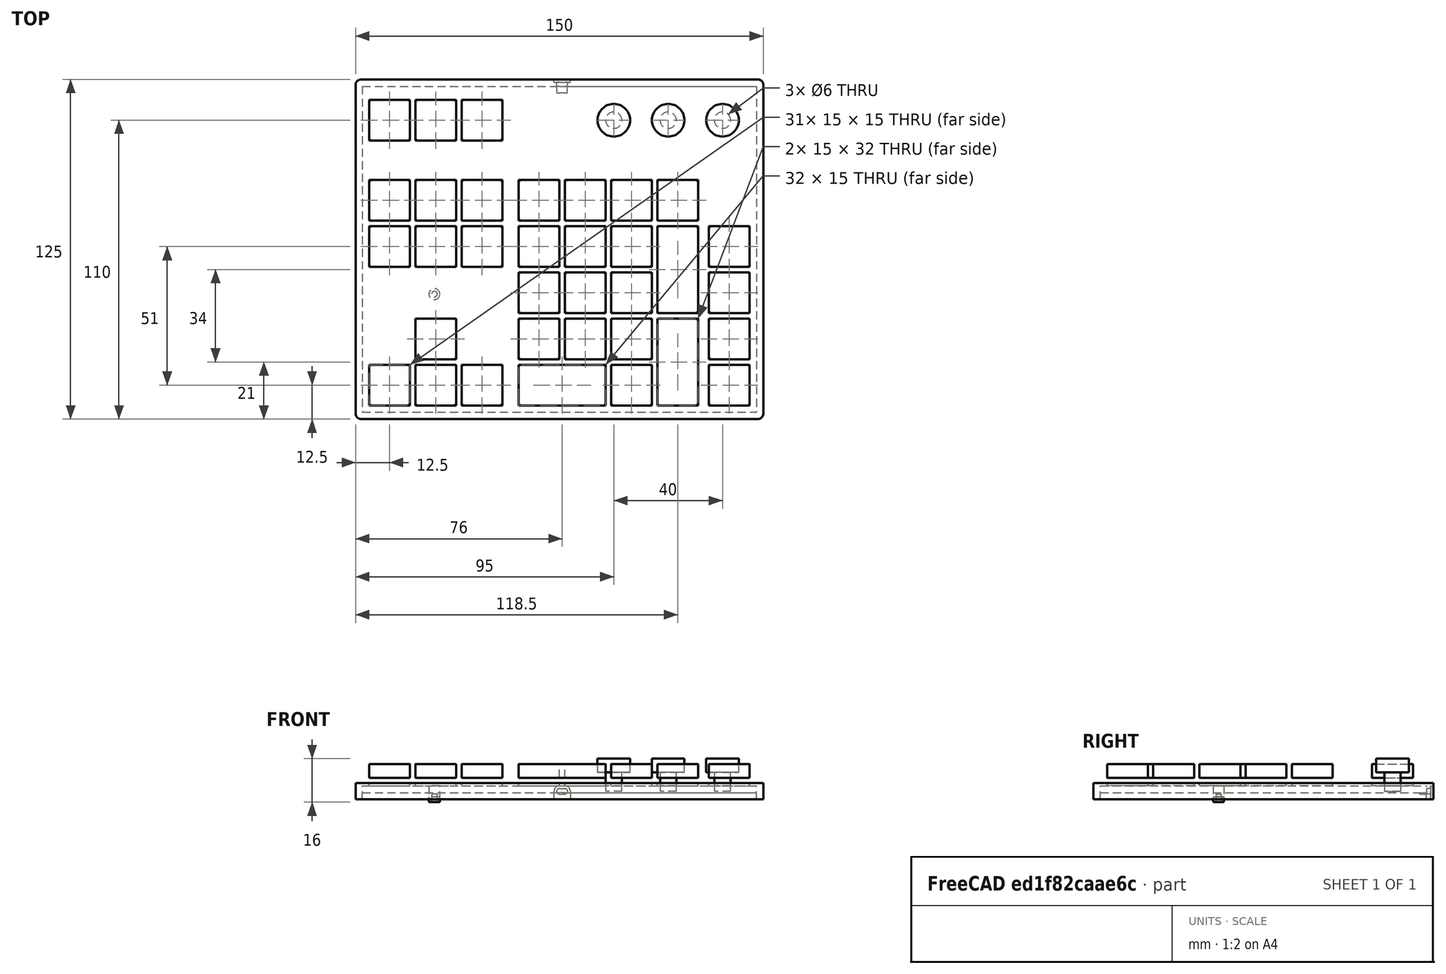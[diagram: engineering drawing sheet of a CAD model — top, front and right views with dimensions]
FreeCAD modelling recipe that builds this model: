
FCSTD DOCUMENT  (FreeCAD 1.0R39109 (Git))
Label: control
License: All rights reserved
LicenseURL: https://en.wikipedia.org/wiki/All_rights_reserved
objects: Part::Box×76, Part::Cut×42, Part::Fillet×35, Part::Cylinder×18, App::DocumentObjectGroup×5, Part::MultiFuse×3
note: 174 computed .brp shape members not serialized (recipe doc carries the construction recipe); baked Part::Feature solids carry a one-line shape summary decoded from their .brp

FEATURE [Part::Box] Box002  label="Down-S"
  AttacherType = Attacher::AttachEngine3D
  Height = 5
  Length = 15
  Placement = pos=(22,5,12) rot=(0,0,1;0rad)
  Width = 15
FEATURE [Part::Box] Box003  label="Up-S"
  AttacherType = Attacher::AttachEngine3D
  Height = 5
  Length = 15
  Placement = pos=(22,22,12) rot=(0,0,1;0rad)
  Width = 15
FEATURE [Part::Box] Box004  label="Right-S"
  AttacherType = Attacher::AttachEngine3D
  Height = 5
  Length = 15
  Placement = pos=(39,5,12) rot=(0,0,1;0rad)
  Width = 15
FEATURE [Part::Box] Box005  label="Zero/Insert-S"
  AttacherType = Attacher::AttachEngine3D
  Height = 5
  Length = 32
  Placement = pos=(60,5,12) rot=(0,0,1;0rad)
  Width = 15
FEATURE [Part::Box] Box006  label="Delete-S"
  AttacherType = Attacher::AttachEngine3D
  Height = 5
  Length = 15
  Placement = pos=(94,5,12) rot=(0,0,1;0rad)
  Width = 15
FEATURE [Part::Box] Box007  label="Left-S"
  AttacherType = Attacher::AttachEngine3D
  Height = 5
  Length = 15
  Placement = pos=(5,5,12) rot=(0,0,1;0rad)
  Width = 15
FEATURE [Part::Box] Box  label="Platform"
  AttacherType = Attacher::AttachEngine3D
  Height = 10
  Length = 150
  Width = 125
FEATURE [Part::Box] Box008  label="End-S"
  AttacherType = Attacher::AttachEngine3D
  Height = 5
  Length = 15
  Placement = pos=(130,5,12) rot=(0,0,1;0rad)
  Width = 15
FEATURE [Part::Fillet] Fillet
  Base = -> Box
  EdgeLinks = -> Box [Edge1,Edge3,Edge5,Edge7]
  Edges = 4 edges r=2: [Edge1,Edge3,Edge5,Edge7]
FEATURE [Part::Box] Box009  label="One-S"
  AttacherType = Attacher::AttachEngine3D
  Height = 5
  Length = 15
  Placement = pos=(60,22,12) rot=(0,0,1;0rad)
  Width = 15
FEATURE [Part::Box] Box010  label="Two-S"
  AttacherType = Attacher::AttachEngine3D
  Height = 5
  Length = 15
  Placement = pos=(77,22,12) rot=(0,0,1;0rad)
  Width = 15
FEATURE [Part::Box] Box011  label="Three-S"
  AttacherType = Attacher::AttachEngine3D
  Height = 5
  Length = 15
  Placement = pos=(94,22,12) rot=(0,0,1;0rad)
  Width = 15
FEATURE [Part::Box] Box012  label="Four-S"
  AttacherType = Attacher::AttachEngine3D
  Height = 5
  Length = 15
  Placement = pos=(60,39,12) rot=(0,0,1;0rad)
  Width = 15
FEATURE [Part::Box] Box013  label="Five-S"
  AttacherType = Attacher::AttachEngine3D
  Height = 5
  Length = 15
  Placement = pos=(77,39,12) rot=(0,0,1;0rad)
  Width = 15
FEATURE [Part::Box] Box014  label="Six-S"
  AttacherType = Attacher::AttachEngine3D
  Height = 5
  Length = 15
  Placement = pos=(94,39,12) rot=(0,0,1;0rad)
  Width = 15
FEATURE [Part::Box] Box015  label="Nine-S"
  AttacherType = Attacher::AttachEngine3D
  Height = 5
  Length = 15
  Placement = pos=(94,56,12) rot=(0,0,1;0rad)
  Width = 15
FEATURE [Part::Box] Box016  label="Eight-S"
  AttacherType = Attacher::AttachEngine3D
  Height = 5
  Length = 15
  Placement = pos=(77,56,12) rot=(0,0,1;0rad)
  Width = 15
FEATURE [Part::Box] Box017  label="Seven-S"
  AttacherType = Attacher::AttachEngine3D
  Height = 5
  Length = 15
  Placement = pos=(60,56,12) rot=(0,0,1;0rad)
  Width = 15
FEATURE [Part::Box] Box018  label="Numlock-S"
  AttacherType = Attacher::AttachEngine3D
  Height = 5
  Length = 15
  Placement = pos=(60,73,12) rot=(0,0,1;0rad)
  Width = 15
FEATURE [Part::Box] Box019  label="Divide-S"
  AttacherType = Attacher::AttachEngine3D
  Height = 5
  Length = 15
  Placement = pos=(77,73,12) rot=(0,0,1;0rad)
  Width = 15
FEATURE [Part::Box] Box020  label="Multi-S"
  AttacherType = Attacher::AttachEngine3D
  Height = 5
  Length = 15
  Placement = pos=(94,73,12) rot=(0,0,1;0rad)
  Width = 15
FEATURE [Part::Box] Box021  label="Enter-S"
  AttacherType = Attacher::AttachEngine3D
  Height = 5
  Length = 15
  Placement = pos=(111,5,12) rot=(0,0,1;0rad)
  Width = 32
FEATURE [Part::Box] Box022  label="PgDn-S"
  AttacherType = Attacher::AttachEngine3D
  Height = 5
  Length = 15
  Placement = pos=(130,22,12) rot=(0,0,1;0rad)
  Width = 15
FEATURE [Part::Box] Box023  label="Plus-S"
  AttacherType = Attacher::AttachEngine3D
  Height = 5
  Length = 15
  Placement = pos=(111,39,12) rot=(0,0,1;0rad)
  Width = 32
FEATURE [Part::Box] Box024  label="Minus-S"
  AttacherType = Attacher::AttachEngine3D
  Height = 5
  Length = 15
  Placement = pos=(111,73,12) rot=(0,0,1;0rad)
  Width = 15
FEATURE [Part::Box] Box025  label="PgUp-S"
  AttacherType = Attacher::AttachEngine3D
  Height = 5
  Length = 15
  Placement = pos=(130,39,12) rot=(0,0,1;0rad)
  Width = 15
FEATURE [Part::Box] Box026  label="Home-S"
  AttacherType = Attacher::AttachEngine3D
  Height = 5
  Length = 15
  Placement = pos=(130,56,12) rot=(0,0,1;0rad)
  Width = 15
FEATURE [Part::Box] Box027  label="M3"
  AttacherType = Attacher::AttachEngine3D
  Height = 5
  Length = 15
  Placement = pos=(39,56,12) rot=(0,0,1;0rad)
  Width = 15
FEATURE [Part::Cylinder] Cylinder
  Angle = 180
  AttacherType = Attacher::AttachEngine3D
  FirstAngle = 0
  Height = 3
  Placement = pos=(77,126,6) rot=(0.58,0.58,-0.58;2.0944rad)
  Radius = 1
  SecondAngle = 0
FEATURE [Part::Box] Box028  label="Up002"
  AttacherType = Attacher::AttachEngine3D
  Height = 10
  Length = 15
  Placement = pos=(22,22,5) rot=(0,0,1;0rad)
  Width = 15
FEATURE [Part::Cut] Cut
  Base = -> Fillet
  Tool = -> Box028
FEATURE [Part::Box] Box029  label="Down001"
  AttacherType = Attacher::AttachEngine3D
  Height = 10
  Length = 15
  Placement = pos=(22,5,5) rot=(0,0,1;0rad)
  Width = 15
FEATURE [Part::Cut] Cut001
  Base = -> Cut
  Tool = -> Box029
FEATURE [Part::Box] Box030  label="Left001"
  AttacherType = Attacher::AttachEngine3D
  Height = 10
  Length = 15
  Placement = pos=(5,5,5) rot=(0,0,1;0rad)
  Width = 15
FEATURE [Part::Cut] Cut002
  Base = -> Cut001
  Tool = -> Box030
FEATURE [Part::Box] Box031  label="Right001"
  AttacherType = Attacher::AttachEngine3D
  Height = 10
  Length = 15
  Placement = pos=(39,5,5) rot=(0,0,1;0rad)
  Width = 15
FEATURE [Part::Cut] Cut003
  Base = -> Cut002
  Tool = -> Box031
FEATURE [Part::Box] Box032  label="Zero/Insert001"
  AttacherType = Attacher::AttachEngine3D
  Height = 10
  Length = 32
  Placement = pos=(60,5,5) rot=(0,0,1;0rad)
  Width = 15
FEATURE [Part::Cut] Cut004
  Base = -> Cut003
  Tool = -> Box032
FEATURE [Part::Box] Box033  label="Delete001"
  AttacherType = Attacher::AttachEngine3D
  Height = 10
  Length = 15
  Placement = pos=(94,5,5) rot=(0,0,1;0rad)
  Width = 15
FEATURE [Part::Cut] Cut005
  Base = -> Cut004
  Tool = -> Box033
FEATURE [Part::Box] Box034  label="One001"
  AttacherType = Attacher::AttachEngine3D
  Height = 10
  Length = 15
  Placement = pos=(60,22,5) rot=(0,0,1;0rad)
  Width = 15
FEATURE [Part::Cut] Cut006
  Base = -> Cut005
  Tool = -> Box034
FEATURE [Part::Box] Box035  label="Two001"
  AttacherType = Attacher::AttachEngine3D
  Height = 10
  Length = 15
  Placement = pos=(77,22,5) rot=(0,0,1;0rad)
  Width = 15
FEATURE [Part::Cut] Cut007
  Base = -> Cut006
  Tool = -> Box035
FEATURE [Part::Box] Box036  label="Three001"
  AttacherType = Attacher::AttachEngine3D
  Height = 10
  Length = 15
  Placement = pos=(94,22,5) rot=(0,0,1;0rad)
  Width = 15
FEATURE [Part::Cut] Cut008
  Base = -> Cut007
  Tool = -> Box036
FEATURE [Part::Box] Box037  label="Four001"
  AttacherType = Attacher::AttachEngine3D
  Height = 10
  Length = 15
  Placement = pos=(60,39,5) rot=(0,0,1;0rad)
  Width = 15
FEATURE [Part::Cut] Cut009
  Base = -> Cut008
  Tool = -> Box037
FEATURE [Part::Box] Box038  label="Five001"
  AttacherType = Attacher::AttachEngine3D
  Height = 10
  Length = 15
  Placement = pos=(77,39,5) rot=(0,0,1;0rad)
  Width = 15
FEATURE [Part::Cut] Cut010
  Base = -> Cut009
  Tool = -> Box038
FEATURE [Part::Box] Box039  label="Six001"
  AttacherType = Attacher::AttachEngine3D
  Height = 10
  Length = 15
  Placement = pos=(94,39,5) rot=(0,0,1;0rad)
  Width = 15
FEATURE [Part::Cut] Cut011
  Base = -> Cut010
  Tool = -> Box039
FEATURE [Part::Box] Box040  label="Seven001"
  AttacherType = Attacher::AttachEngine3D
  Height = 10
  Length = 15
  Placement = pos=(60,56,5) rot=(0,0,1;0rad)
  Width = 15
FEATURE [Part::Cut] Cut012
  Base = -> Cut011
  Tool = -> Box040
FEATURE [Part::Box] Box041  label="Eight001"
  AttacherType = Attacher::AttachEngine3D
  Height = 10
  Length = 15
  Placement = pos=(77,56,5) rot=(0,0,1;0rad)
  Width = 15
FEATURE [Part::Cut] Cut013
  Base = -> Cut012
  Tool = -> Box041
FEATURE [Part::Box] Box042  label="Nine001"
  AttacherType = Attacher::AttachEngine3D
  Height = 10
  Length = 15
  Placement = pos=(94,56,5) rot=(0,0,1;0rad)
  Width = 15
FEATURE [Part::Cut] Cut014
  Base = -> Cut013
  Tool = -> Box042
FEATURE [Part::Box] Box043  label="Numlock001"
  AttacherType = Attacher::AttachEngine3D
  Height = 10
  Length = 15
  Placement = pos=(60,73,5) rot=(0,0,1;0rad)
  Width = 15
FEATURE [Part::Cut] Cut015
  Base = -> Cut014
  Tool = -> Box043
FEATURE [Part::Box] Box044  label="Divide001"
  AttacherType = Attacher::AttachEngine3D
  Height = 10
  Length = 15
  Placement = pos=(77,73,5) rot=(0,0,1;0rad)
  Width = 15
FEATURE [Part::Cut] Cut016
  Base = -> Cut015
  Tool = -> Box044
FEATURE [Part::Box] Box045  label="Multi001"
  AttacherType = Attacher::AttachEngine3D
  Height = 10
  Length = 15
  Placement = pos=(94,73,5) rot=(0,0,1;0rad)
  Width = 15
FEATURE [Part::Cut] Cut017
  Base = -> Cut016
  Tool = -> Box045
FEATURE [Part::Box] Box046  label="Enter001"
  AttacherType = Attacher::AttachEngine3D
  Height = 10
  Length = 15
  Placement = pos=(111,5,5) rot=(0,0,1;0rad)
  Width = 32
FEATURE [Part::Cut] Cut018
  Base = -> Cut017
  Tool = -> Box046
FEATURE [Part::Box] Box047  label="Plus001"
  AttacherType = Attacher::AttachEngine3D
  Height = 10
  Length = 15
  Placement = pos=(111,39,5) rot=(0,0,1;0rad)
  Width = 32
FEATURE [Part::Cut] Cut019
  Base = -> Cut018
  Tool = -> Box047
FEATURE [Part::Box] Box048  label="Minus001"
  AttacherType = Attacher::AttachEngine3D
  Height = 10
  Length = 15
  Placement = pos=(111,73,5) rot=(0,0,1;0rad)
  Width = 15
FEATURE [Part::Cut] Cut020
  Base = -> Cut019
  Tool = -> Box048
FEATURE [Part::Box] Box049  label="Home001"
  AttacherType = Attacher::AttachEngine3D
  Height = 10
  Length = 15
  Placement = pos=(130,56,5) rot=(0,0,1;0rad)
  Width = 15
FEATURE [Part::Cut] Cut021
  Base = -> Cut020
  Tool = -> Box049
FEATURE [Part::Box] Box050  label="PgUp001"
  AttacherType = Attacher::AttachEngine3D
  Height = 10
  Length = 15
  Placement = pos=(130,39,5) rot=(0,0,1;0rad)
  Width = 15
FEATURE [Part::Cut] Cut022
  Base = -> Cut021
  Tool = -> Box050
FEATURE [Part::Box] Box051  label="PgDn001"
  AttacherType = Attacher::AttachEngine3D
  Height = 10
  Length = 15
  Placement = pos=(130,22,5) rot=(0,0,1;0rad)
  Width = 15
FEATURE [Part::Cut] Cut023
  Base = -> Cut022
  Tool = -> Box051
FEATURE [Part::Box] Box052  label="End001"
  AttacherType = Attacher::AttachEngine3D
  Height = 10
  Length = 15
  Placement = pos=(130,5,5) rot=(0,0,1;0rad)
  Width = 15
FEATURE [Part::Cut] Cut024
  Base = -> Cut023
  Tool = -> Box052
FEATURE [Part::Box] Box053  label="M2"
  AttacherType = Attacher::AttachEngine3D
  Height = 5
  Length = 15
  Placement = pos=(22,56,12) rot=(0,0,1;0rad)
  Width = 15
FEATURE [Part::Box] Box054  label="M1"
  AttacherType = Attacher::AttachEngine3D
  Height = 5
  Length = 15
  Placement = pos=(5,56,12) rot=(0,0,1;0rad)
  Width = 15
FEATURE [Part::Box] Box055  label="M4"
  AttacherType = Attacher::AttachEngine3D
  Height = 5
  Length = 15
  Placement = pos=(5,73,12) rot=(0,0,1;0rad)
  Width = 15
FEATURE [Part::Box] Box056  label="M5"
  AttacherType = Attacher::AttachEngine3D
  Height = 5
  Length = 15
  Placement = pos=(22,73,12) rot=(0,0,1;0rad)
  Width = 15
FEATURE [Part::Box] Box057  label="M6"
  AttacherType = Attacher::AttachEngine3D
  Height = 5
  Length = 15
  Placement = pos=(39,73,12) rot=(0,0,1;0rad)
  Width = 15
FEATURE [Part::Box] Box058  label="M007"
  AttacherType = Attacher::AttachEngine3D
  Height = 10
  Length = 15
  Placement = pos=(5,56,5) rot=(0,0,1;0rad)
  Width = 15
FEATURE [Part::Cut] Cut025
  Base = -> Cut024
  Tool = -> Box058
FEATURE [Part::Box] Box059  label="M008"
  AttacherType = Attacher::AttachEngine3D
  Height = 10
  Length = 15
  Placement = pos=(22,56,5) rot=(0,0,1;0rad)
  Width = 15
FEATURE [Part::Cut] Cut026
  Base = -> Cut025
  Tool = -> Box059
FEATURE [Part::Box] Box060  label="M009"
  AttacherType = Attacher::AttachEngine3D
  Height = 10
  Length = 15
  Placement = pos=(39,56,5) rot=(0,0,1;0rad)
  Width = 15
FEATURE [Part::Cut] Cut027
  Base = -> Cut026
  Tool = -> Box060
FEATURE [Part::Box] Box061  label="M010"
  AttacherType = Attacher::AttachEngine3D
  Height = 10
  Length = 15
  Placement = pos=(5,73,5) rot=(0,0,1;0rad)
  Width = 15
FEATURE [Part::Cut] Cut028
  Base = -> Cut027
  Tool = -> Box061
FEATURE [Part::Box] Box062  label="M011"
  AttacherType = Attacher::AttachEngine3D
  Height = 10
  Length = 15
  Placement = pos=(22,73,5) rot=(0,0,1;0rad)
  Width = 15
FEATURE [Part::Cut] Cut029
  Base = -> Cut028
  Tool = -> Box062
FEATURE [Part::Box] Box063  label="M012"
  AttacherType = Attacher::AttachEngine3D
  Height = 10
  Length = 15
  Placement = pos=(39,73,5) rot=(0,0,1;0rad)
  Width = 15
FEATURE [Part::Cut] Cut030
  Base = -> Cut029
  Tool = -> Box063
FEATURE [Part::Cylinder] Cylinder001  label="Stick 1"
  Angle = 360
  AttacherType = Attacher::AttachEngine3D
  FirstAngle = 0
  Height = 10
  Placement = pos=(135,110,5) rot=(0,0,1;0rad)
  Radius = 3
  SecondAngle = 0
FEATURE [Part::Cylinder] Cylinder002  label="Stick 2"
  Angle = 360
  AttacherType = Attacher::AttachEngine3D
  FirstAngle = 0
  Height = 10
  Placement = pos=(115,110,5) rot=(0,0,1;0rad)
  Radius = 3
  SecondAngle = 0
FEATURE [Part::Cylinder] Cylinder003  label="Top 1"
  Angle = 360
  AttacherType = Attacher::AttachEngine3D
  FirstAngle = 0
  Height = 5
  Placement = pos=(135,110,14) rot=(0,0,1;0rad)
  Radius = 6
  SecondAngle = 0
FEATURE [Part::Cylinder] Cylinder004  label="Top 2"
  Angle = 360
  AttacherType = Attacher::AttachEngine3D
  FirstAngle = 0
  Height = 5
  Placement = pos=(115,110,14) rot=(0,0,1;0rad)
  Radius = 6
  SecondAngle = 0
FEATURE [Part::Box] Box064  label="M7"
  AttacherType = Attacher::AttachEngine3D
  Height = 5
  Length = 15
  Placement = pos=(5,102.5,12) rot=(0,0,1;0rad)
  Width = 15
FEATURE [Part::Box] Box065  label="M8"
  AttacherType = Attacher::AttachEngine3D
  Height = 5
  Length = 15
  Placement = pos=(22,102.5,12) rot=(0,0,1;0rad)
  Width = 15
FEATURE [Part::Box] Box066  label="M9"
  AttacherType = Attacher::AttachEngine3D
  Height = 5
  Length = 15
  Placement = pos=(39,102.5,12) rot=(0,0,1;0rad)
  Width = 15
FEATURE [Part::Cylinder] Cylinder005  label="Stick 3"
  Angle = 360
  AttacherType = Attacher::AttachEngine3D
  FirstAngle = 0
  Height = 10
  Placement = pos=(95,110,5) rot=(0,0,1;0rad)
  Radius = 3
  SecondAngle = 0
FEATURE [Part::Cylinder] Cylinder006  label="Top 3"
  Angle = 360
  AttacherType = Attacher::AttachEngine3D
  FirstAngle = 0
  Height = 5
  Placement = pos=(95,110,14) rot=(0,0,1;0rad)
  Radius = 6
  SecondAngle = 0
FEATURE [Part::Box] Box067  label="M013"
  AttacherType = Attacher::AttachEngine3D
  Height = 10
  Length = 15
  Placement = pos=(22,102.5,5) rot=(0,0,1;0rad)
  Width = 15
FEATURE [Part::Cut] Cut031
  Base = -> Cut030
  Tool = -> Box067
FEATURE [Part::Box] Box068  label="M014"
  AttacherType = Attacher::AttachEngine3D
  Height = 10
  Length = 15
  Placement = pos=(39,102.5,5) rot=(0,0,1;0rad)
  Width = 15
FEATURE [Part::Cut] Cut032
  Base = -> Cut031
  Tool = -> Box068
FEATURE [Part::Box] Box069  label="M015"
  AttacherType = Attacher::AttachEngine3D
  Height = 10
  Length = 15
  Placement = pos=(5,102.5,5) rot=(0,0,1;0rad)
  Width = 15
FEATURE [Part::Cut] Cut033
  Base = -> Cut032
  Tool = -> Box069
FEATURE [Part::Fillet] Fillet001  label="Up-R"
  Base = -> Box003
  EdgeLinks = -> Box003 [Edge1,Edge3,Edge5,Edge7]
  Edges = 4 edges r=1: [Edge1,Edge3,Edge5,Edge7]
FEATURE [Part::Fillet] Fillet002  label="Left-R"
  Base = -> Box007
  EdgeLinks = -> Box007 [Edge1,Edge3,Edge5,Edge7]
  Edges = 4 edges r=1: [Edge1,Edge3,Edge5,Edge7]
FEATURE [Part::Fillet] Fillet003  label="Right-R"
  Base = -> Box004
  EdgeLinks = -> Box004 [Edge1,Edge3,Edge5,Edge7]
  Edges = 4 edges r=1: [Edge1,Edge3,Edge5,Edge7]
FEATURE [Part::Fillet] Fillet004  label="Down-R"
  Base = -> Box002
  EdgeLinks = -> Box002 [Edge1,Edge3,Edge5,Edge7]
  Edges = 4 edges r=1: [Edge1,Edge3,Edge5,Edge7]
FEATURE [App::DocumentObjectGroup] Group  label="Arrows"
  Group = -> [Box003,Fillet001,Box002,Fillet004,Box007,Fillet002,Box004,Fillet003]
FEATURE [Part::Fillet] Fillet005  label="Zero/Insert-R"
  Base = -> Box005
  EdgeLinks = -> Box005 [Edge1,Edge3,Edge5,Edge7]
  Edges = 4 edges r=1: [Edge1,Edge3,Edge5,Edge7]
FEATURE [Part::Fillet] Fillet006  label="Delete-R"
  Base = -> Box006
  EdgeLinks = -> Box006 [Edge1,Edge3,Edge5,Edge7]
  Edges = 4 edges r=1: [Edge1,Edge3,Edge5,Edge7]
FEATURE [Part::Fillet] Fillet007  label="One-R"
  Base = -> Box009
  EdgeLinks = -> Box009 [Edge1,Edge3,Edge5,Edge7]
  Edges = 4 edges r=1: [Edge1,Edge3,Edge5,Edge7]
FEATURE [Part::Fillet] Fillet008  label="Two-R"
  Base = -> Box010
  EdgeLinks = -> Box010 [Edge1,Edge3,Edge5,Edge7]
  Edges = 4 edges r=1: [Edge1,Edge3,Edge5,Edge7]
FEATURE [Part::Fillet] Fillet009  label="Three-R"
  Base = -> Box011
  EdgeLinks = -> Box011 [Edge1,Edge3,Edge5,Edge7]
  Edges = 4 edges r=1: [Edge1,Edge3,Edge5,Edge7]
FEATURE [Part::Fillet] Fillet010  label="Four-R"
  Base = -> Box012
  EdgeLinks = -> Box012 [Edge1,Edge3,Edge5,Edge7]
  Edges = 4 edges r=1: [Edge1,Edge3,Edge5,Edge7]
FEATURE [Part::Fillet] Fillet011  label="Five-R"
  Base = -> Box013
  EdgeLinks = -> Box013 [Edge1,Edge3,Edge5,Edge7]
  Edges = 4 edges r=1: [Edge1,Edge3,Edge5,Edge7]
FEATURE [Part::Fillet] Fillet012  label="Six-R"
  Base = -> Box014
  EdgeLinks = -> Box014 [Edge1,Edge3,Edge5,Edge7]
  Edges = 4 edges r=1: [Edge1,Edge3,Edge5,Edge7]
FEATURE [Part::Fillet] Fillet013  label="Seven-R"
  Base = -> Box017
  EdgeLinks = -> Box017 [Edge1,Edge3,Edge5,Edge7]
  Edges = 4 edges r=1: [Edge1,Edge3,Edge5,Edge7]
FEATURE [Part::Fillet] Fillet014  label="Eight-R"
  Base = -> Box016
  EdgeLinks = -> Box016 [Edge1,Edge3,Edge5,Edge7]
  Edges = 4 edges r=1: [Edge1,Edge3,Edge5,Edge7]
FEATURE [Part::Fillet] Fillet015  label="Nine-R"
  Base = -> Box015
  EdgeLinks = -> Box015 [Edge1,Edge3,Edge5,Edge7]
  Edges = 4 edges r=1: [Edge1,Edge3,Edge5,Edge7]
FEATURE [Part::Fillet] Fillet016  label="Numlock-R"
  Base = -> Box018
  EdgeLinks = -> Box018 [Edge1,Edge3,Edge5,Edge7]
  Edges = 4 edges r=1: [Edge1,Edge3,Edge5,Edge7]
FEATURE [Part::Fillet] Fillet017  label="Divide-R"
  Base = -> Box019
  EdgeLinks = -> Box019 [Edge1,Edge3,Edge5,Edge7]
  Edges = 4 edges r=1: [Edge1,Edge3,Edge5,Edge7]
FEATURE [Part::Fillet] Fillet018  label="Multi-R"
  Base = -> Box020
  EdgeLinks = -> Box020 [Edge1,Edge3,Edge5,Edge7]
  Edges = 4 edges r=1: [Edge1,Edge3,Edge5,Edge7]
FEATURE [Part::Fillet] Fillet019  label="Enter-R"
  Base = -> Box021
  EdgeLinks = -> Box021 [Edge1,Edge3,Edge5,Edge7]
  Edges = 4 edges r=1: [Edge1,Edge3,Edge5,Edge7]
FEATURE [Part::Fillet] Fillet020  label="Plus-R"
  Base = -> Box023
  EdgeLinks = -> Box023 [Edge1,Edge3,Edge5,Edge7]
  Edges = 4 edges r=1: [Edge1,Edge3,Edge5,Edge7]
FEATURE [Part::Fillet] Fillet021  label="Minus-R"
  Base = -> Box024
  EdgeLinks = -> Box024 [Edge1,Edge3,Edge5,Edge7]
  Edges = 4 edges r=1: [Edge1,Edge3,Edge5,Edge7]
FEATURE [App::DocumentObjectGroup] Group001  label="Numpad"
  Group = -> [Box005,Fillet005,Box006,Fillet006,Box009,Fillet007,Box010,Fillet008,Box011,Fillet009,Box012,Fillet010,Box013,Fillet011,Box014,Fillet012,Box017,Fillet013,Box016,Fillet014,Box015,Fillet015,Box018,Fillet016,Box019,Fillet017,Box020,Fillet018,Box021,Fillet019,Box023,Fillet020,Box024,Fillet021]
FEATURE [Part::Fillet] Fillet022  label="Home-R"
  Base = -> Box026
  EdgeLinks = -> Box026 [Edge1,Edge3,Edge5,Edge7]
  Edges = 4 edges r=1: [Edge1,Edge3,Edge5,Edge7]
FEATURE [Part::Fillet] Fillet023  label="PgUp-R"
  Base = -> Box025
  EdgeLinks = -> Box025 [Edge1,Edge3,Edge5,Edge7]
  Edges = 4 edges r=1: [Edge1,Edge3,Edge5,Edge7]
FEATURE [Part::Fillet] Fillet024  label="PgDn-R"
  Base = -> Box022
  EdgeLinks = -> Box022 [Edge1,Edge3,Edge5,Edge7]
  Edges = 4 edges r=1: [Edge1,Edge3,Edge5,Edge7]
FEATURE [Part::Fillet] Fillet025  label="End-R"
  Base = -> Box008
  EdgeLinks = -> Box008 [Edge1,Edge3,Edge5,Edge7]
  Edges = 4 edges r=1: [Edge1,Edge3,Edge5,Edge7]
FEATURE [App::DocumentObjectGroup] Group002  label="Home-End"
  Group = -> [Box026,Fillet022,Box025,Fillet023,Box022,Fillet024,Box008,Fillet025]
FEATURE [Part::Fillet] Fillet026  label="M1-R"
  Base = -> Box054
  EdgeLinks = -> Box054 [Edge1,Edge3,Edge5,Edge7]
  Edges = 4 edges r=1: [Edge1,Edge3,Edge5,Edge7]
FEATURE [Part::Fillet] Fillet027  label="M2-R"
  Base = -> Box053
  EdgeLinks = -> Box053 [Edge1,Edge3,Edge5,Edge7]
  Edges = 4 edges r=1: [Edge1,Edge3,Edge5,Edge7]
FEATURE [Part::Fillet] Fillet028  label="M3-R"
  Base = -> Box027
  EdgeLinks = -> Box027 [Edge1,Edge3,Edge5,Edge7]
  Edges = 4 edges r=1: [Edge1,Edge3,Edge5,Edge7]
FEATURE [Part::Fillet] Fillet029  label="M4-R"
  Base = -> Box055
  EdgeLinks = -> Box055 [Edge1,Edge3,Edge5,Edge7]
  Edges = 4 edges r=1: [Edge1,Edge3,Edge5,Edge7]
FEATURE [Part::Fillet] Fillet030  label="M5-R"
  Base = -> Box056
  EdgeLinks = -> Box056 [Edge1,Edge3,Edge5,Edge7]
  Edges = 4 edges r=1: [Edge1,Edge3,Edge5,Edge7]
FEATURE [Part::Fillet] Fillet031  label="M6-R"
  Base = -> Box057
  EdgeLinks = -> Box057 [Edge1,Edge3,Edge5,Edge7]
  Edges = 4 edges r=1: [Edge1,Edge3,Edge5,Edge7]
FEATURE [Part::Fillet] Fillet032  label="M7-R"
  Base = -> Box064
  EdgeLinks = -> Box064 [Edge1,Edge3,Edge5,Edge7]
  Edges = 4 edges r=1: [Edge1,Edge3,Edge5,Edge7]
FEATURE [Part::Fillet] Fillet033  label="M8-R"
  Base = -> Box065
  EdgeLinks = -> Box065 [Edge1,Edge3,Edge5,Edge7]
  Edges = 4 edges r=1: [Edge1,Edge3,Edge5,Edge7]
FEATURE [Part::Fillet] Fillet034  label="M9-R"
  Base = -> Box066
  EdgeLinks = -> Box066 [Edge1,Edge3,Edge5,Edge7]
  Edges = 4 edges r=1: [Edge1,Edge3,Edge5,Edge7]
FEATURE [App::DocumentObjectGroup] Group003  label="Macros"
  Group = -> [Box054,Fillet026,Box053,Fillet027,Box027,Fillet028,Box055,Fillet029,Box056,Fillet030,Box057,Fillet031,Box064,Fillet032,Box065,Fillet033,Box066,Fillet034]
FEATURE [Part::Box] Box070  label="Cube"
  AttacherType = Attacher::AttachEngine3D
  Height = 9
  Length = 145
  Placement = pos=(2.5,2.5,0) rot=(0,0,1;0rad)
  Width = 120
FEATURE [Part::Box] Box071  label="Cube001"
  AttacherType = Attacher::AttachEngine3D
  Height = 2.5
  Length = 145
  Placement = pos=(2.5,2.5,4) rot=(0,0,1;0rad)
  Width = 120
FEATURE [Part::Cut] Cut034  label="Frame"
  Base = -> Cut033
  Tool = -> Box070
FEATURE [Part::Cylinder] Cylinder007
  Angle = 180
  AttacherType = Attacher::AttachEngine3D
  FirstAngle = 0
  Height = 3
  Placement = pos=(75,126,6) rot=(-0.58,0.58,-0.58;4.18879rad)
  Radius = 1
  SecondAngle = 0
FEATURE [Part::Box] Box072  label="Cube002"
  AttacherType = Attacher::AttachEngine3D
  Height = 2
  Length = 2
  Placement = pos=(75,123,5) rot=(0,0,1;0rad)
  Width = 3
FEATURE [Part::MultiFuse] Fusion  label="USB-C Port"
  Placement = pos=(0,-1,1) rot=(0,0,1;0rad)
  Shapes = -> [Cylinder,Box072,Cylinder007]
FEATURE [Part::Box] Box073  label="Cube003"
  AttacherType = Attacher::AttachEngine3D
  Height = 4
  Length = 150
  Width = 125
FEATURE [Part::Cut] Cut035  label="Top Frame"
  Base = -> Cut034
  Tool = -> Box073
FEATURE [Part::Box] Box074  label="Cube004"
  AttacherType = Attacher::AttachEngine3D
  Height = 4
  Length = 2
  Placement = pos=(75,124,5) rot=(0,0,1;0rad)
  Width = 2
FEATURE [Part::Cylinder] Cylinder008
  Angle = 180
  AttacherType = Attacher::AttachEngine3D
  FirstAngle = 0
  Height = 2
  Placement = pos=(77,126,7) rot=(0.58,0.58,-0.58;2.0944rad)
  Radius = 2
  SecondAngle = 0
FEATURE [Part::Cylinder] Cylinder009
  Angle = 180
  AttacherType = Attacher::AttachEngine3D
  FirstAngle = 0
  Height = 2
  Placement = pos=(75,126,7) rot=(-0.58,0.58,-0.58;4.18879rad)
  Radius = 2
  SecondAngle = 0
FEATURE [Part::Box] Box075  label="Cube005"
  AttacherType = Attacher::AttachEngine3D
  Height = 3
  Length = 6
  Placement = pos=(73,124,4) rot=(0,0,1;0rad)
  Width = 2
FEATURE [Part::MultiFuse] Fusion001
  Shapes = -> [Cylinder008,Box074,Cylinder009,Box075]
FEATURE [Part::Cut] Cut036
  Base = -> Cut035
  Tool = -> Fusion001
FEATURE [Part::Cut] Cut037  label="Frame001"
  Base = -> Cut036
  Tool = -> Fusion
FEATURE [Part::Cylinder] Cylinder010  label="Stick 004"
  Angle = 360
  AttacherType = Attacher::AttachEngine3D
  FirstAngle = 0
  Height = 7
  Placement = pos=(135,110,7) rot=(0,0,1;0rad)
  Radius = 3
  SecondAngle = 0
FEATURE [Part::Cylinder] Cylinder011  label="Stick 005"
  Angle = 360
  AttacherType = Attacher::AttachEngine3D
  FirstAngle = 0
  Height = 7
  Placement = pos=(115,110,7) rot=(0,0,1;0rad)
  Radius = 3
  SecondAngle = 0
FEATURE [Part::Cylinder] Cylinder012  label="Stick 006"
  Angle = 360
  AttacherType = Attacher::AttachEngine3D
  FirstAngle = 0
  Height = 7
  Placement = pos=(95,110,7) rot=(0,0,1;0rad)
  Radius = 3
  SecondAngle = 0
FEATURE [App::DocumentObjectGroup] Group004  label="Rotaries"
  Group = -> [Cylinder003,Cylinder010,Cylinder004,Cylinder011,Cylinder006,Cylinder012]
FEATURE [Part::Cut] Cut038
  Base = -> Cut037
  Tool = -> Cylinder001
FEATURE [Part::Cut] Cut039
  Base = -> Cut038
  Tool = -> Cylinder002
FEATURE [Part::Cut] Cut040  label="Upper Housing"
  Base = -> Cut039
  Tool = -> Cylinder005
FEATURE [Part::Box] Box076  label="Cube006"
  AttacherType = Attacher::AttachEngine3D
  Height = 2
  Length = 2
  Placement = pos=(75,123,5) rot=(0,0,1;0rad)
  Width = 3
FEATURE [Part::Cylinder] Cylinder013
  Angle = 180
  AttacherType = Attacher::AttachEngine3D
  FirstAngle = 0
  Height = 3
  Placement = pos=(77,126,6) rot=(0.58,0.58,-0.58;2.0944rad)
  Radius = 1
  SecondAngle = 0
FEATURE [Part::Cylinder] Cylinder014
  Angle = 180
  AttacherType = Attacher::AttachEngine3D
  FirstAngle = 0
  Height = 3
  Placement = pos=(75,126,6) rot=(-0.58,0.58,-0.58;4.18879rad)
  Radius = 1
  SecondAngle = 0
FEATURE [Part::MultiFuse] Fusion002  label="USB-C Port001"
  Placement = pos=(0,-3,1) rot=(0,0,1;0rad)
  Shapes = -> [Cylinder013,Box076,Cylinder014]
FEATURE [Part::Cut] Cut041  label="Lower Housing"
  Base = -> Box071
  Tool = -> Fusion002
FEATURE [Part::Cylinder] Cylinder015
  Angle = 360
  AttacherType = Attacher::AttachEngine3D
  FirstAngle = 0
  Height = 6
  Placement = pos=(29,46,3) rot=(0,0,1;0rad)
  Radius = 2
  SecondAngle = 0
FEATURE [Part::Cylinder] Cylinder016
  Angle = 360
  AttacherType = Attacher::AttachEngine3D
  FirstAngle = 0
  Height = 3
  Placement = pos=(29,46,3) rot=(0,0,1;0rad)
  Radius = 1
  SecondAngle = 0
FEATURE [Part::Cylinder] Cylinder017
  Angle = 360
  AttacherType = Attacher::AttachEngine3D
  FirstAngle = 0
  Height = 2
  Placement = pos=(29,46,3) rot=(0,0,1;0rad)
  Radius = 2
  SecondAngle = 0
